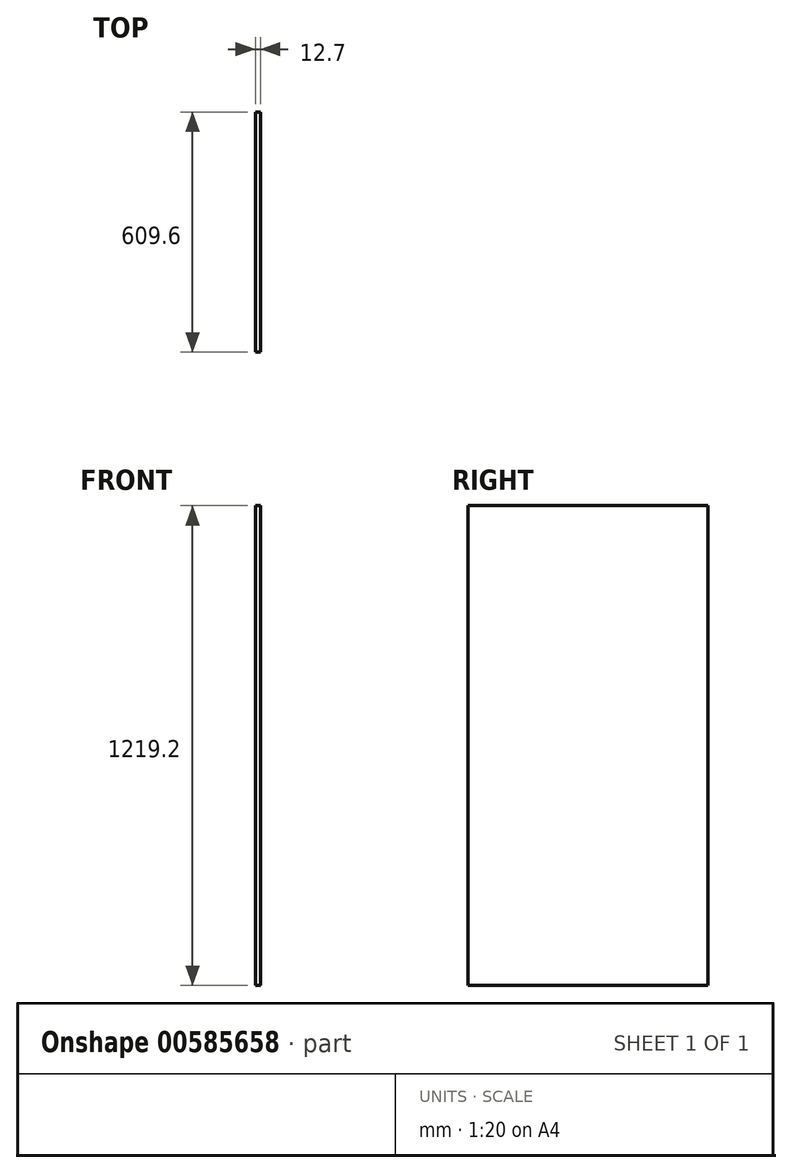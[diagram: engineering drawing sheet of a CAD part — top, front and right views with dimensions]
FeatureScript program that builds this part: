
annotation { "Feature Type Name" : "Feature", "Feature Type Description" : "" }
export const myFeature = defineFeature(function(context is Context, id is Id, definition is map)
    precondition{}
    {
        {
            var Q0;
            Q0=qCreatedBy(makeId("Right.planeOp"),FACE);
            var sketch = newSketch(context, id + "F0", { "sketchPlane" : qUnion([Q0])});
            skLineSegment(sketch, "E0.bottom", {"start": v(0, 0) * mm, "end": v(609.6, 0) * mm});
            skLineSegment(sketch, "E0.top", {"start": v(0, 1219.2) * mm, "end": v(609.6, 1219.2) * mm});
            skLineSegment(sketch, "E0.left", {"start": v(0, 0) * mm, "end": v(0, 1219.2) * mm});
            skLineSegment(sketch, "E0.right", {"start": v(609.6, 0) * mm, "end": v(609.6, 1219.2) * mm});
            skSolve(sketch);
        }
        {
            var Q0;
            Q0=qSketchRegion(id+"F0",true);
            extrude(context, id + "F1", {"entities" : qUnion([Q0]), "depth" : 12.7 * mm, "offsetDistance" : 25.4 * mm});
        }
    });
